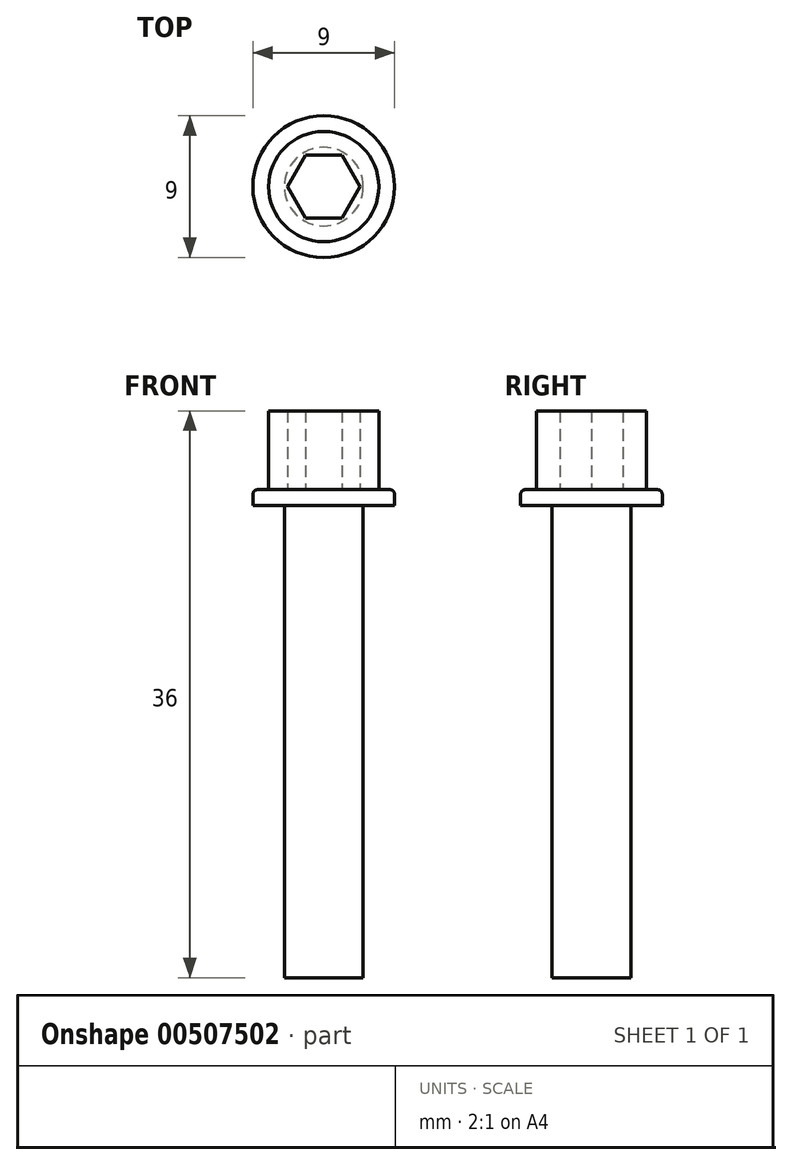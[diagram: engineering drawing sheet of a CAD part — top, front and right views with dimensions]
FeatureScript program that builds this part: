
annotation { "Feature Type Name" : "Feature", "Feature Type Description" : "" }
export const myFeature = defineFeature(function(context is Context, id is Id, definition is map)
    precondition{}
    {
        {
            var Q0;
            Q0=qCreatedBy(makeId("Top.planeOp"),FACE);
            var sketch = newSketch(context, id + "F0", { "sketchPlane" : qUnion([Q0])});
            skCircle(sketch, "E0", {"center": v(0, 0) * mm, "radius": 3.5 * mm});
            skCircle(sketch, "E1.cCircle", {"center": v(0, 0) * mm, "radius": 2 * mm, "construction": true});
            skLineSegment(sketch, "E1.0", {"start": v(-1.15, 2) * mm, "end": v(1.15, 2) * mm});
            skLineSegment(sketch, "E1.1", {"start": v(1.15, 2) * mm, "end": v(2.3, 0) * mm});
            skLineSegment(sketch, "E1.2", {"start": v(2.3, 0) * mm, "end": v(1.15, -2) * mm});
            skLineSegment(sketch, "E1.3", {"start": v(1.15, -2) * mm, "end": v(-1.15, -2) * mm});
            skLineSegment(sketch, "E1.4", {"start": v(-1.15, -2) * mm, "end": v(-2.3, 0) * mm});
            skLineSegment(sketch, "E1.5", {"start": v(-2.3, 0) * mm, "end": v(-1.15, 2) * mm});
            skPoint(sketch, "E1.0.midPoint", {"position": v(0, 2) * mm});
            skSolve(sketch);
        }
        {
            var Q0;
            Q0=makeQuery(id+"F0.imprint","IMPRINT",FACE,{"disambiguationData":[TD([[makeQuery(id+"F0.imprint","IMPRINT",EDGE,{"derivedFrom":sQuery(id+"F0.wireOp",EDGE,"E0")}),1.0]])]});
            extrude(context, id + "F1", {"entities" : qUnion([Q0]), "depth" : 5 * mm});
        }
        {
            var Q0;
            Q0=makeQuery(id+"F1.opExtrude","CAP_FACE",FACE,{"disambiguationData":[OSD([sQuery(id+"F0.wireOp",EDGE,"E0"),sQuery(id+"F0.wireOp",EDGE,"E1.0"),sQuery(id+"F0.wireOp",EDGE,"E1.1"),sQuery(id+"F0.wireOp",EDGE,"E1.2"),sQuery(id+"F0.wireOp",EDGE,"E1.3"),sQuery(id+"F0.wireOp",EDGE,"E1.4"),sQuery(id+"F0.wireOp",EDGE,"E1.5")])],"isStart":true});
            var sketch = newSketch(context, id + "F2", { "sketchPlane" : qUnion([Q0])});
            skCircle(sketch, "E2", {"center": v(0, 0) * mm, "radius": 4.5 * mm});
            skSolve(sketch);
        }
        {
            var Q0;
            Q0 = qSketchRegion(id + "F2", true);
            extrude(context, id + "F3", {"entities" : qUnion([Q0]), "operationType" : NewBodyOperationType.ADD, "depth" : (1) * mm});
        }
        {
            var Q0;
            Q0=makeQuery(id+"F3.opExtrude","CAP_FACE",FACE,{"disambiguationData":[OSD([sQuery(id+"F2.wireOp",EDGE,"E2")])],"isStart":false});
            var sketch = newSketch(context, id + "F4", { "sketchPlane" : qUnion([Q0])});
            skCircle(sketch, "E3", {"center": v(0, 0) * mm, "radius": 2.5 * mm});
            skSolve(sketch);
        }
        {
            var Q0;
            Q0 = qSketchRegion(id + "F4", true);
            extrude(context, id + "F5", {"entities" : qUnion([Q0]), "operationType" : NewBodyOperationType.ADD, "depth" : 30 * mm});
        }
        {
            var Q0;
            Q0=makeQuery(id+"F3.opExtrude","CAP_EDGE",EDGE,{"disambiguationData":[OSD([sQuery(id+"F2.wireOp",EDGE,"E2")])],"isStart":true});
            fillet(context, id + "F6", {"entities" : qUnion([Q0]), "radius" : 0.3 * mm, "tangentPropagation" : true, "allowEdgeOverflow" : false});
        }
    });
